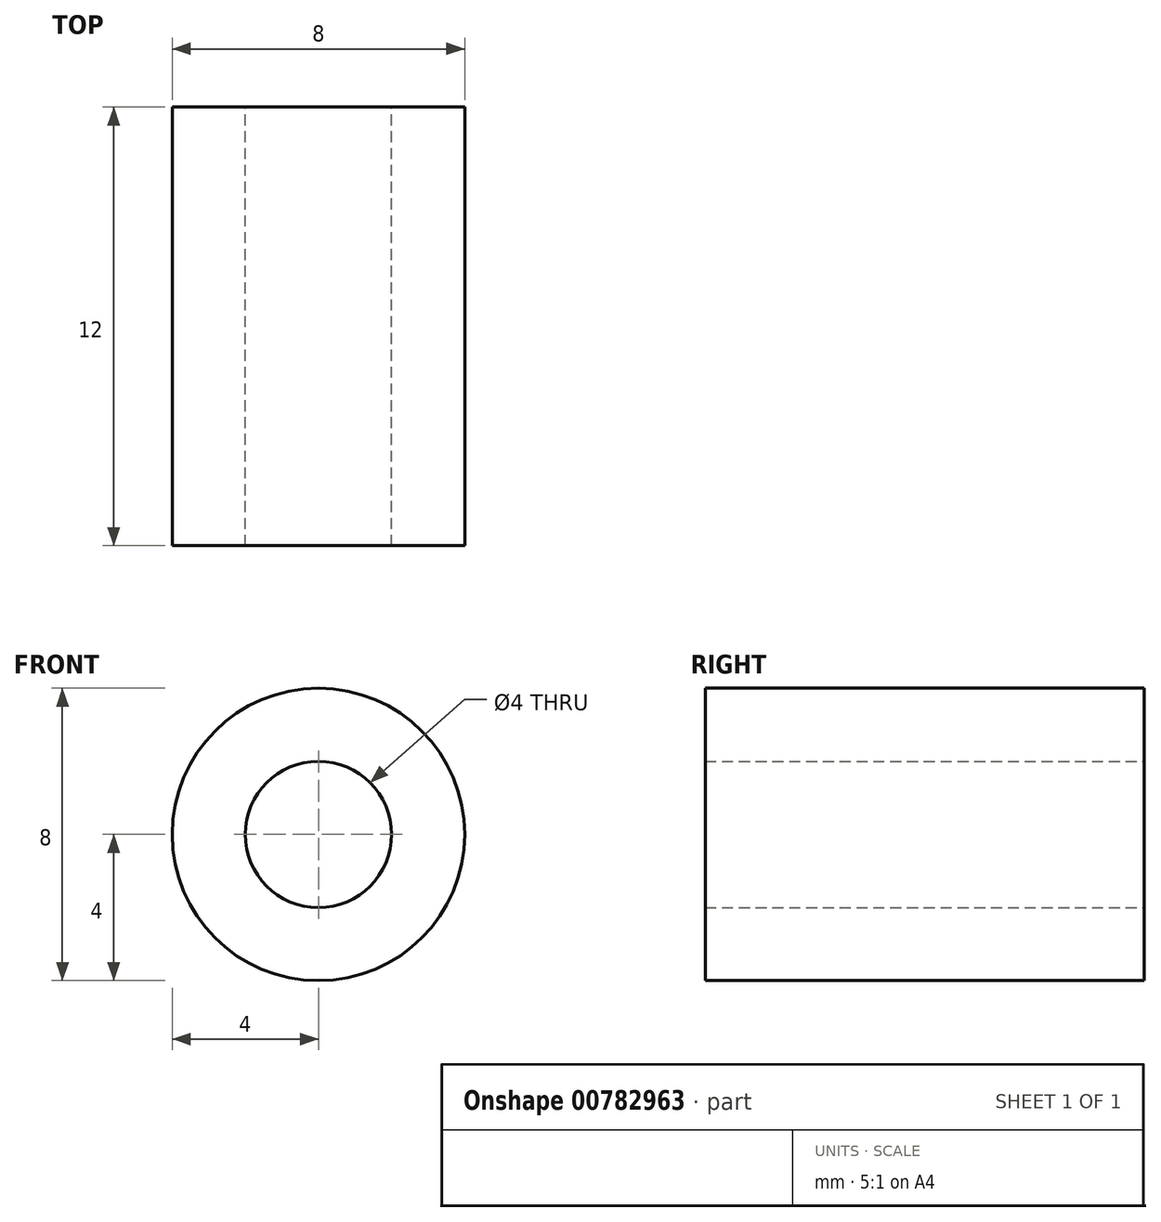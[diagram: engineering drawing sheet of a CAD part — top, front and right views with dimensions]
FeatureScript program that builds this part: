
annotation { "Feature Type Name" : "Feature", "Feature Type Description" : "" }
export const myFeature = defineFeature(function(context is Context, id is Id, definition is map)
    precondition{}
    {
        {
            var Q0;
            Q0=qCreatedBy(makeId("Front.planeOp"),FACE);
            var sketch = newSketch(context, id + "F0", { "sketchPlane" : qUnion([Q0])});
            skCircle(sketch, "E0", {"center": v(0, 0) * mm, "radius": 4 * mm});
            skCircle(sketch, "E1", {"center": v(0, 0) * mm, "radius": 2 * mm});
            skSolve(sketch);
        }
        {
            var Q0;
            Q0=qSketchRegion(id+"F0",true);
            extrude(context, id + "F1", {"entities" : qUnion([Q0]), "depth" : 12 * mm, "offsetDistance" : 25 * mm});
        }
    });
